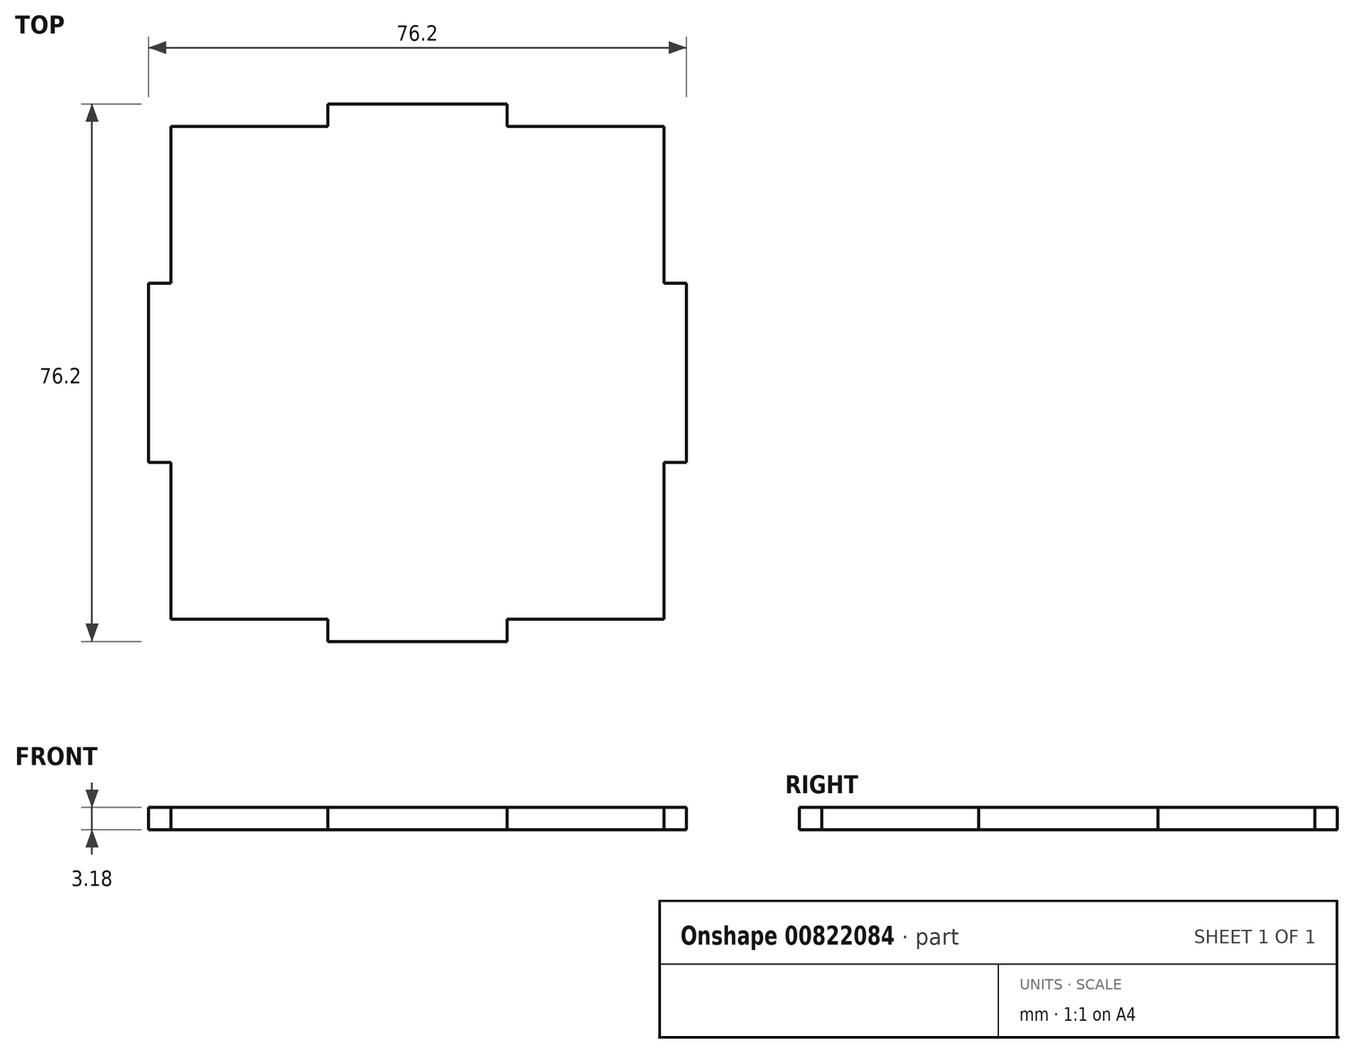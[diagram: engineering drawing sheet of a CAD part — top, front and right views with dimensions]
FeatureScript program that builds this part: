
annotation { "Feature Type Name" : "Feature", "Feature Type Description" : "" }
export const myFeature = defineFeature(function(context is Context, id is Id, definition is map)
    precondition{}
    {
        {
            var Q0;
            Q0=qCreatedBy(makeId("Top.planeOp"),FACE);
            var sketch = newSketch(context, id + "F0", { "sketchPlane" : qUnion([Q0])});
            skLineSegment(sketch, "E0.bottom", {"start": v(-38.1, 38.1) * mm, "end": v(38.1, 38.1) * mm});
            skLineSegment(sketch, "E0.top", {"start": v(-38.1, -38.1) * mm, "end": v(38.1, -38.1) * mm});
            skLineSegment(sketch, "E0.left", {"start": v(-38.1, 38.1) * mm, "end": v(-38.1, -38.1) * mm});
            skLineSegment(sketch, "E0.right", {"start": v(38.1, 38.1) * mm, "end": v(38.1, -38.1) * mm});
            skPoint(sketch, "E0.middle", {"position": v(0, 0) * mm});
            skSolve(sketch);
        }
        {
            var Q0;
            Q0 = qSketchRegion(id + "F0", true);
            extrude(context, id + "F1", {"entities" : qUnion([Q0]), "depth" : 3.17 * mm, "offsetDistance" : 25.4 * mm});
        }
        {
            var Q0;
            Q0=makeQuery(id+"F1.opExtrude","CAP_FACE",FACE,{"disambiguationData":[OSD([sQuery(id+"F0.wireOp",EDGE,"E0.bottom"),sQuery(id+"F0.wireOp",EDGE,"E0.top"),sQuery(id+"F0.wireOp",EDGE,"E0.left"),sQuery(id+"F0.wireOp",EDGE,"E0.right")])],"isStart":false});
            var sketch = newSketch(context, id + "F2", { "sketchPlane" : qUnion([Q0])});
            skLineSegment(sketch, "E1.bottom", {"start": v(-38.1, 38.1) * mm, "end": v(-34.92, 38.1) * mm});
            skLineSegment(sketch, "E1.top", {"start": v(-38.1, 12.7) * mm, "end": v(-34.92, 12.7) * mm});
            skLineSegment(sketch, "E1.left", {"start": v(-38.1, 38.1) * mm, "end": v(-38.1, 12.7) * mm});
            skLineSegment(sketch, "E1.right", {"start": v(-34.92, 38.1) * mm, "end": v(-34.92, 12.7) * mm});
            skLineSegment(sketch, "E2.0.1.0", {"start": v(-38.1, -12.7) * mm, "end": v(-34.92, -12.7) * mm});
            skLineSegment(sketch, "E2.0.1.1", {"start": v(-38.1, -38.1) * mm, "end": v(-34.92, -38.1) * mm});
            skLineSegment(sketch, "E2.0.1.2", {"start": v(-38.1, -12.7) * mm, "end": v(-38.1, -38.1) * mm});
            skLineSegment(sketch, "E2.0.1.3", {"start": v(-34.92, -12.7) * mm, "end": v(-34.92, -38.1) * mm});
            skLineSegment(sketch, "E2.direction1", {"start": v(-38.1, 12.7) * mm, "end": v(-12.7, 12.7) * mm, "construction": true});
            skLineSegment(sketch, "E2.direction2", {"start": v(-38.1, 12.7) * mm, "end": v(-38.1, -38.1) * mm, "construction": true});
            skLineSegment(sketch, "E3.1.0", {"start": v(-38.1, -34.92) * mm, "end": v(-12.7, -34.92) * mm});
            skLineSegment(sketch, "E3.1.1", {"start": v(-38.1, -38.1) * mm, "end": v(-12.7, -38.1) * mm});
            skLineSegment(sketch, "E3.1.2", {"start": v(12.7, -34.92) * mm, "end": v(38.1, -34.92) * mm});
            skLineSegment(sketch, "E3.1.3", {"start": v(-12.7, -38.1) * mm, "end": v(38.1, -38.1) * mm, "construction": true});
            skLineSegment(sketch, "E3.1.4", {"start": v(12.7, -38.1) * mm, "end": v(38.1, -38.1) * mm});
            skLineSegment(sketch, "E3.1.5", {"start": v(38.1, -38.1) * mm, "end": v(38.1, -34.92) * mm});
            skLineSegment(sketch, "E3.1.6", {"start": v(12.7, -38.1) * mm, "end": v(12.7, -34.92) * mm});
            skLineSegment(sketch, "E3.1.7", {"start": v(-12.7, -38.1) * mm, "end": v(-12.7, -34.92) * mm});
            skLineSegment(sketch, "E3.1.8", {"start": v(-38.1, -38.1) * mm, "end": v(-38.1, -34.92) * mm});
            skLineSegment(sketch, "E3.2.0", {"start": v(34.92, -38.1) * mm, "end": v(34.92, -12.7) * mm});
            skLineSegment(sketch, "E3.2.1", {"start": v(38.1, -38.1) * mm, "end": v(38.1, -12.7) * mm});
            skLineSegment(sketch, "E3.2.2", {"start": v(34.93, 12.7) * mm, "end": v(34.93, 38.1) * mm});
            skLineSegment(sketch, "E3.2.3", {"start": v(38.1, -12.7) * mm, "end": v(38.1, 38.1) * mm, "construction": true});
            skLineSegment(sketch, "E3.2.4", {"start": v(38.1, 12.7) * mm, "end": v(38.1, 38.1) * mm});
            skLineSegment(sketch, "E3.2.5", {"start": v(38.1, 38.1) * mm, "end": v(34.93, 38.1) * mm});
            skLineSegment(sketch, "E3.2.6", {"start": v(38.1, 12.7) * mm, "end": v(34.92, 12.7) * mm});
            skLineSegment(sketch, "E3.2.7", {"start": v(38.1, -12.7) * mm, "end": v(34.92, -12.7) * mm});
            skLineSegment(sketch, "E3.2.8", {"start": v(38.1, -38.1) * mm, "end": v(34.92, -38.1) * mm});
            skLineSegment(sketch, "E3.3.0", {"start": v(38.1, 34.92) * mm, "end": v(12.7, 34.92) * mm});
            skLineSegment(sketch, "E3.3.1", {"start": v(38.1, 38.1) * mm, "end": v(12.7, 38.1) * mm});
            skLineSegment(sketch, "E3.3.2", {"start": v(-12.7, 34.92) * mm, "end": v(-38.1, 34.93) * mm});
            skLineSegment(sketch, "E3.3.3", {"start": v(12.7, 38.1) * mm, "end": v(-38.1, 38.1) * mm, "construction": true});
            skLineSegment(sketch, "E3.3.4", {"start": v(-12.7, 38.1) * mm, "end": v(-38.1, 38.1) * mm});
            skLineSegment(sketch, "E3.3.5", {"start": v(-38.1, 38.1) * mm, "end": v(-38.1, 34.93) * mm});
            skLineSegment(sketch, "E3.3.6", {"start": v(-12.7, 38.1) * mm, "end": v(-12.7, 34.92) * mm});
            skLineSegment(sketch, "E3.3.7", {"start": v(12.7, 38.1) * mm, "end": v(12.7, 34.92) * mm});
            skLineSegment(sketch, "E3.3.8", {"start": v(38.1, 38.1) * mm, "end": v(38.1, 34.92) * mm});
            skPoint(sketch, "E3.center", {"position": v(0, 0) * mm});
            skSolve(sketch);
        }
        {
            var Q0;
            Q0 = qSketchRegion(id + "F2", true);
            extrude(context, id + "F3", {"entities" : qUnion([Q0]), "operationType" : NewBodyOperationType.REMOVE, "oppositeDirection" : true, "depth" : 25.4 * mm, "offsetDistance" : 25.4 * mm});
        }
    });
